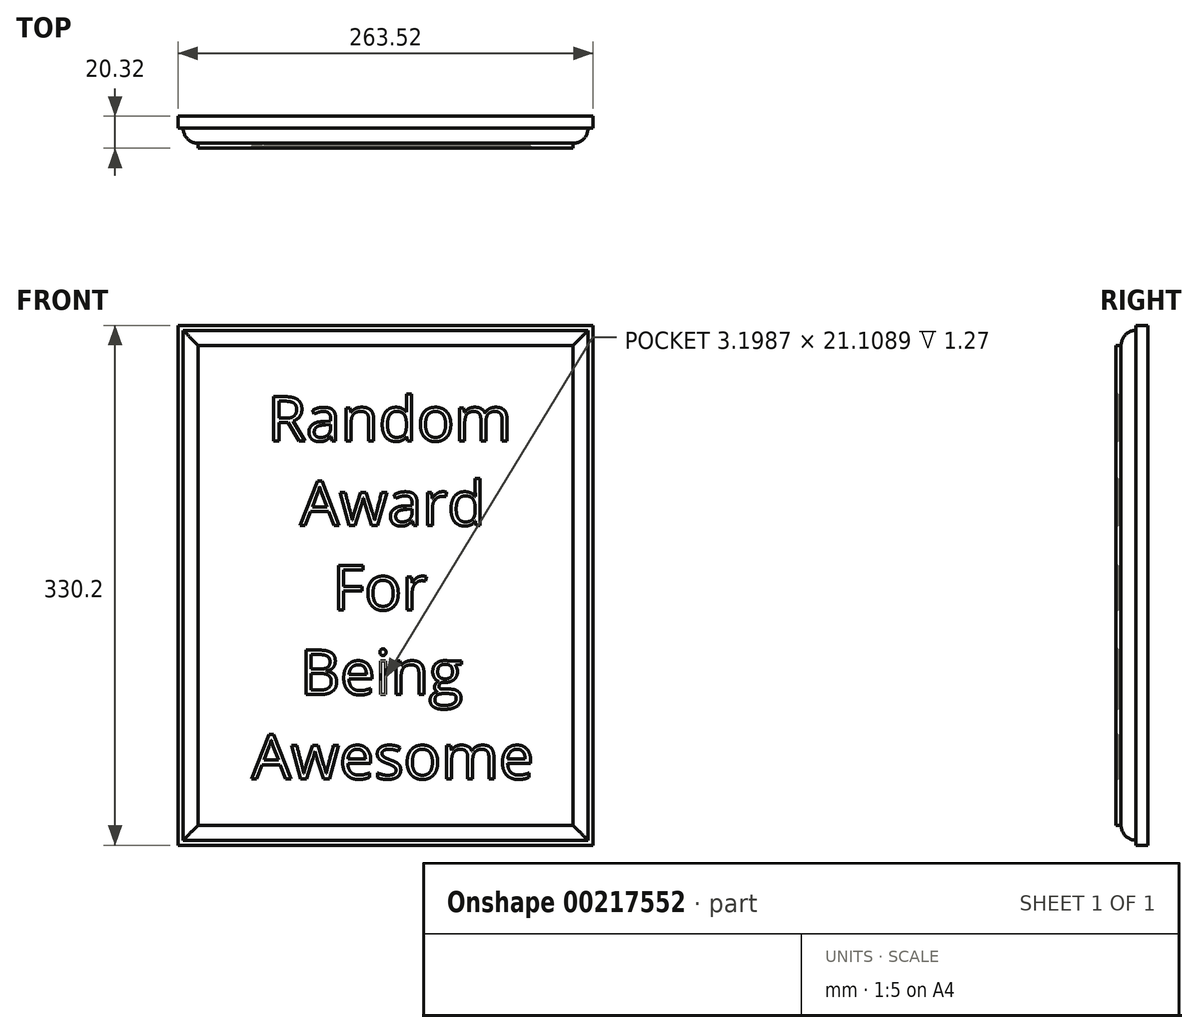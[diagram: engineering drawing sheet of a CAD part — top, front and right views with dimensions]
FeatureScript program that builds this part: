
annotation { "Feature Type Name" : "Feature", "Feature Type Description" : "" }
export const myFeature = defineFeature(function(context is Context, id is Id, definition is map)
    precondition{}
    {
        {
            var Q0;
            Q0=qCreatedBy(makeId("Front.planeOp"),FACE);
            var sketch = newSketch(context, id + "F0", { "sketchPlane" : qUnion([Q0])});
            skLineSegment(sketch, "E0.bottom", {"start": v(-131.76, 165.1) * mm, "end": v(131.76, 165.1) * mm});
            skLineSegment(sketch, "E0.top", {"start": v(-131.76, -165.1) * mm, "end": v(131.76, -165.1) * mm});
            skLineSegment(sketch, "E0.left", {"start": v(-131.76, 165.1) * mm, "end": v(-131.76, -165.1) * mm});
            skLineSegment(sketch, "E0.right", {"start": v(131.76, 165.1) * mm, "end": v(131.76, -165.1) * mm});
            skSolve(sketch);
        }
        {
            var Q0;
            Q0=makeQuery(id+"F0.imprint","IMPRINT",FACE,{"disambiguationData":[TD([[makeQuery(id+"F0.imprint","IMPRINT",EDGE,{"derivedFrom":sQuery(id+"F0.wireOp",EDGE,"E0.bottom")}),-1.0]])]});
            extrude(context, id + "F1", {"entities" : qUnion([Q0]), "oppositeDirection" : true, "depth" : 20.32 * mm});
        }
        {
            var Q0;
            Q0=makeQuery(id+"F1.opExtrude","SWEPT_FACE",FACE,{"disambiguationData":[OSD([sQuery(id+"F0.wireOp",EDGE,"E0.right")])]});
            var sketch = newSketch(context, id + "F2", { "sketchPlane" : qUnion([Q0])});
            skLineSegment(sketch, "E1", {"start": v(12.7, 165.1) * mm, "end": v(12.7, 161.93) * mm});
            skLineSegment(sketch, "E2", {"start": v(12.7, 161.93) * mm, "end": v(12.7, 161.93) * mm});
            skLineSegment(sketch, "E3", {"start": v(3.17, 152.4) * mm, "end": v(3.17, 152.4) * mm});
            skLineSegment(sketch, "E4", {"start": v(3.18, 152.4) * mm, "end": v(0, 152.4) * mm});
            skLineSegment(sketch, "E5", {"start": v(0, 152.4) * mm, "end": v(0, 165.1) * mm});
            skLineSegment(sketch, "E6", {"start": v(0, 165.1) * mm, "end": v(12.7, 165.1) * mm});
            skPoint(sketch, "E7.visualSharp", {"position": v(3.17, 161.93) * mm});
            skArc(sketch, "E7.filletArc", {"start": v(12.7, 161.93) * mm, "mid": v(5.96, 159.14) * mm, "end": v(3.17, 152.4) * mm});
            skSolve(sketch);
        }
        {
            var Q0;
            Q0=makeQuery(id+"F2.imprint","IMPRINT",FACE,{"disambiguationData":[TD([[makeQuery(id+"F2.imprint","IMPRINT",EDGE,{"derivedFrom":sQuery(id+"F2.wireOp",EDGE,"E1")}),-1.0]])]});
            var Q1;
            Q1=makeQuery(id+"F1.opExtrude","CAP_EDGE",EDGE,{"disambiguationData":[OSD([sQuery(id+"F0.wireOp",EDGE,"E0.bottom")])],"isStart":true});
            var Q2;
            Q2=makeQuery(id+"F1.opExtrude","CAP_EDGE",EDGE,{"disambiguationData":[OSD([sQuery(id+"F0.wireOp",EDGE,"E0.left")])],"isStart":true});
            var Q3;
            Q3=makeQuery(id+"F1.opExtrude","CAP_EDGE",EDGE,{"disambiguationData":[OSD([sQuery(id+"F0.wireOp",EDGE,"E0.top")])],"isStart":true});
            var Q4;
            Q4=makeQuery(id+"F1.opExtrude","CAP_EDGE",EDGE,{"disambiguationData":[OSD([sQuery(id+"F0.wireOp",EDGE,"E0.right")])],"isStart":true});
            sweep(context, id + "F3", {"operationType" : NewBodyOperationType.REMOVE, "profiles" : qUnion([Q0]), "path" : qUnion([Q1, Q2, Q3, Q4])});
        }
        {
            var Q0;
            Q0=makeQuery(id+"F1.opExtrude","CAP_FACE",FACE,{"disambiguationData":[OSD([sQuery(id+"F0.wireOp",EDGE,"E0.bottom"),sQuery(id+"F0.wireOp",EDGE,"E0.top"),sQuery(id+"F0.wireOp",EDGE,"E0.left"),sQuery(id+"F0.wireOp",EDGE,"E0.right")])],"isStart":true});
            var sketch = newSketch(context, id + "F4", { "sketchPlane" : qUnion([Q0])});
            skText(sketch, "E8", { "text": " Random\n   Award\n     For\n   Being\nAwesome", "fontName": "OpenSans-Regular.ttf"});
            const initialGuessF4  = {"E8": [-0.08512, 0.09163, 1, 0, 0.0284]};
            skSetInitialGuess(sketch, initialGuessF4);
            skSolve(sketch);
        }
        {
            var Q0;
            Q0 = qSketchRegion(id + "F4", true);
            extrude(context, id + "F5", {"entities" : qUnion([Q0]), "operationType" : NewBodyOperationType.REMOVE, "oppositeDirection" : true, "depth" : 1.27 * mm});
        }
    });
